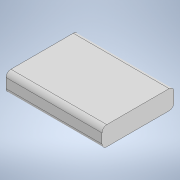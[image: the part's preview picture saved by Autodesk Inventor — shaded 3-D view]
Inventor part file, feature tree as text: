
AUTODESK INVENTOR PART (.ipt)
format: ipt  version: 2022.3 (Build 263350000, 350)  size: 99,328 bytes
history: native  units: mm
features: extrude x1, fillet x1, sketch x1
ambient origin geometry x8: Origin, YZ Plane, XZ Plane, XY Plane, X Axis, Y Axis, Z Axis, Center Point
bodies: Solid1 (feature_tree)
feature tree (3):
  extrude  "Extrusion1"  Depth=15.0mm
  fillet  "Fillet1"  Radius=4.0mm
  sketch  "Sketch1"  dims[d0=20.0mm d1=15.0mm d2=4.0mm d3=0.0mm d4=1.0mm]
